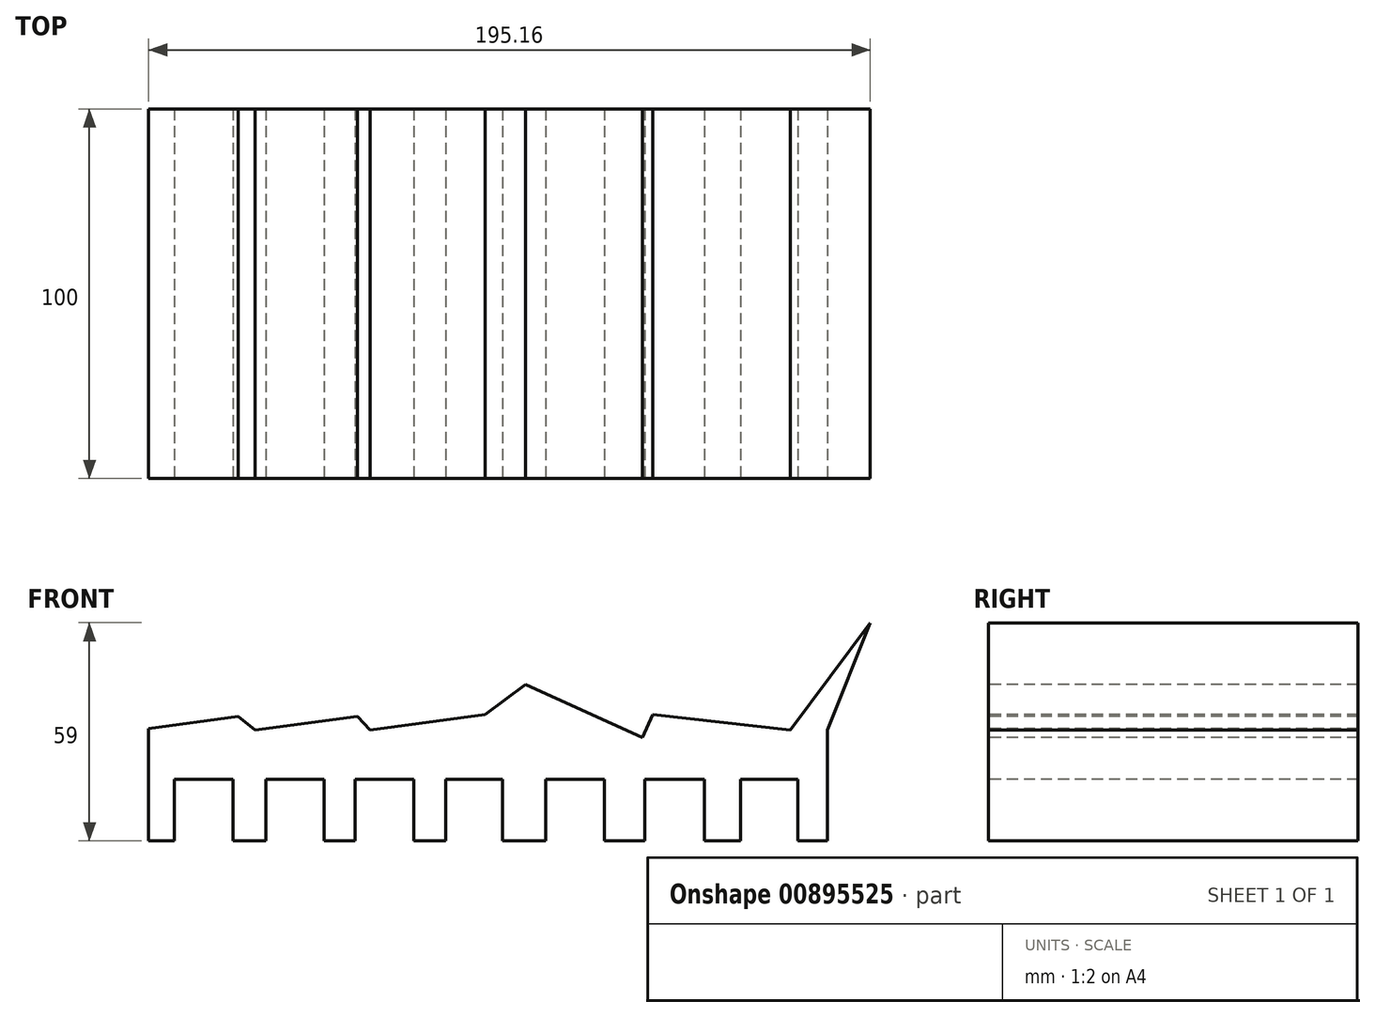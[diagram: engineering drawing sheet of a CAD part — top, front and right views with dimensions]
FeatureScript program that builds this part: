
annotation { "Feature Type Name" : "Feature", "Feature Type Description" : "" }
export const myFeature = defineFeature(function(context is Context, id is Id, definition is map)
    precondition{}
    {
        {
            var Q0;
            Q0=qCreatedBy(makeId("Front.planeOp"),FACE);
            var sketch = newSketch(context, id + "F0", { "sketchPlane" : qUnion([Q0])});
            skLineSegment(sketch, "E0", {"start": v(-99.15, 0) * mm, "end": v(-71.52, 3.72) * mm});
            skLineSegment(sketch, "E1", {"start": v(-71.52, 3.72) * mm, "end": v(-66.91, 0) * mm});
            skLineSegment(sketch, "E2", {"start": v(-66.91, 0) * mm, "end": v(-39.29, 3.72) * mm});
            skLineSegment(sketch, "E3", {"start": v(-39.29, 3.72) * mm, "end": v(-35.83, 0) * mm});
            skLineSegment(sketch, "E4", {"start": v(-35.83, 0) * mm, "end": v(-4.68, 4.2) * mm});
            skLineSegment(sketch, "E5", {"start": v(-4.68, 4.2) * mm, "end": v(6.19, 12.36) * mm});
            skLineSegment(sketch, "E6", {"start": v(6.19, 12.36) * mm, "end": v(37.85, -2.03) * mm});
            skLineSegment(sketch, "E7", {"start": v(37.85, -2.03) * mm, "end": v(40.68, 4.2) * mm});
            skLineSegment(sketch, "E8", {"start": v(40.68, 4.2) * mm, "end": v(77.85, 0) * mm});
            skLineSegment(sketch, "E9", {"start": v(77.85, 0) * mm, "end": v(99.44, 29.05) * mm});
            skLineSegment(sketch, "E10", {"start": v(-99.15, 0) * mm, "end": v(-107.2, 3.15) * mm});
            skLineSegment(sketch, "E11", {"start": v(-95.72, 0.46) * mm, "end": v(-95.72, -29.95) * mm});
            skLineSegment(sketch, "E12", {"start": v(-95.72, -29.95) * mm, "end": v(-88.79, -29.95) * mm});
            skLineSegment(sketch, "E13", {"start": v(-88.79, -29.95) * mm, "end": v(-88.79, -13.26) * mm});
            skLineSegment(sketch, "E14", {"start": v(-88.79, -13.26) * mm, "end": v(-72.96, -13.26) * mm});
            skLineSegment(sketch, "E15", {"start": v(-72.96, -13.26) * mm, "end": v(-72.96, -29.95) * mm});
            skLineSegment(sketch, "E16", {"start": v(-72.96, -29.95) * mm, "end": v(-64.04, -29.95) * mm});
            skLineSegment(sketch, "E17", {"start": v(-64.04, -29.95) * mm, "end": v(-64.04, -13.26) * mm});
            skLineSegment(sketch, "E18", {"start": v(-64.04, -13.26) * mm, "end": v(-48.2, -13.26) * mm});
            skLineSegment(sketch, "E19", {"start": v(-48.2, -13.26) * mm, "end": v(-48.2, -29.95) * mm});
            skLineSegment(sketch, "E20", {"start": v(-48.2, -29.95) * mm, "end": v(-39.86, -29.95) * mm});
            skLineSegment(sketch, "E21", {"start": v(-39.86, -29.95) * mm, "end": v(-39.86, -13.26) * mm});
            skLineSegment(sketch, "E22", {"start": v(-39.86, -13.26) * mm, "end": v(-24.03, -13.26) * mm});
            skLineSegment(sketch, "E23", {"start": v(-24.03, -13.26) * mm, "end": v(-24.03, -29.95) * mm});
            skLineSegment(sketch, "E24", {"start": v(-24.03, -29.95) * mm, "end": v(-15.4, -29.95) * mm});
            skLineSegment(sketch, "E25", {"start": v(-15.4, -29.95) * mm, "end": v(-15.4, -13.26) * mm});
            skLineSegment(sketch, "E26", {"start": v(-15.4, -13.26) * mm, "end": v(0, -13.26) * mm});
            skLineSegment(sketch, "E27", {"start": v(0, -13.26) * mm, "end": v(0, -29.95) * mm});
            skLineSegment(sketch, "E28", {"start": v(0, -29.95) * mm, "end": v(11.66, -29.95) * mm});
            skLineSegment(sketch, "E29", {"start": v(11.66, -29.95) * mm, "end": v(11.66, -13.26) * mm});
            skLineSegment(sketch, "E30", {"start": v(11.66, -13.26) * mm, "end": v(27.49, -13.26) * mm});
            skLineSegment(sketch, "E31", {"start": v(27.49, -13.26) * mm, "end": v(27.49, -29.95) * mm});
            skLineSegment(sketch, "E32", {"start": v(27.49, -29.95) * mm, "end": v(38.42, -29.95) * mm});
            skLineSegment(sketch, "E33", {"start": v(38.42, -29.95) * mm, "end": v(38.42, -13.26) * mm});
            skLineSegment(sketch, "E34", {"start": v(38.42, -13.26) * mm, "end": v(54.54, -13.26) * mm});
            skLineSegment(sketch, "E35", {"start": v(54.54, -13.26) * mm, "end": v(54.54, -29.95) * mm});
            skLineSegment(sketch, "E36", {"start": v(54.54, -29.95) * mm, "end": v(64.32, -29.95) * mm});
            skLineSegment(sketch, "E37", {"start": v(64.32, -29.95) * mm, "end": v(64.32, -13.26) * mm});
            skLineSegment(sketch, "E38", {"start": v(64.32, -13.26) * mm, "end": v(79.87, -13.26) * mm});
            skLineSegment(sketch, "E39", {"start": v(79.87, -13.26) * mm, "end": v(79.87, -29.95) * mm});
            skLineSegment(sketch, "E40", {"start": v(79.87, -29.95) * mm, "end": v(87.92, -29.95) * mm});
            skLineSegment(sketch, "E41", {"start": v(87.92, -29.95) * mm, "end": v(87.92, 0) * mm});
            skLineSegment(sketch, "E42", {"start": v(87.92, 0) * mm, "end": v(99.44, 29.05) * mm});
            skSolve(sketch);
        }
        {
            var Q0;
            {var subQ1=sQuery(id+"F0.wireOp",EDGE,"E1");Q0=makeQuery(id+"F0.imprint","IMPRINT",FACE,{"disambiguationData":[TD([[makeQuery(id+"F0.imprint","IMPRINT",EDGE,{"derivedFrom":subQ1}),-1.0]])]});}
            extrude(context, id + "F1", {"entities" : qUnion([Q0]), "oppositeDirection" : true, "depth" : 100 * mm, "offsetDistance" : 25 * mm});
        }
    });
